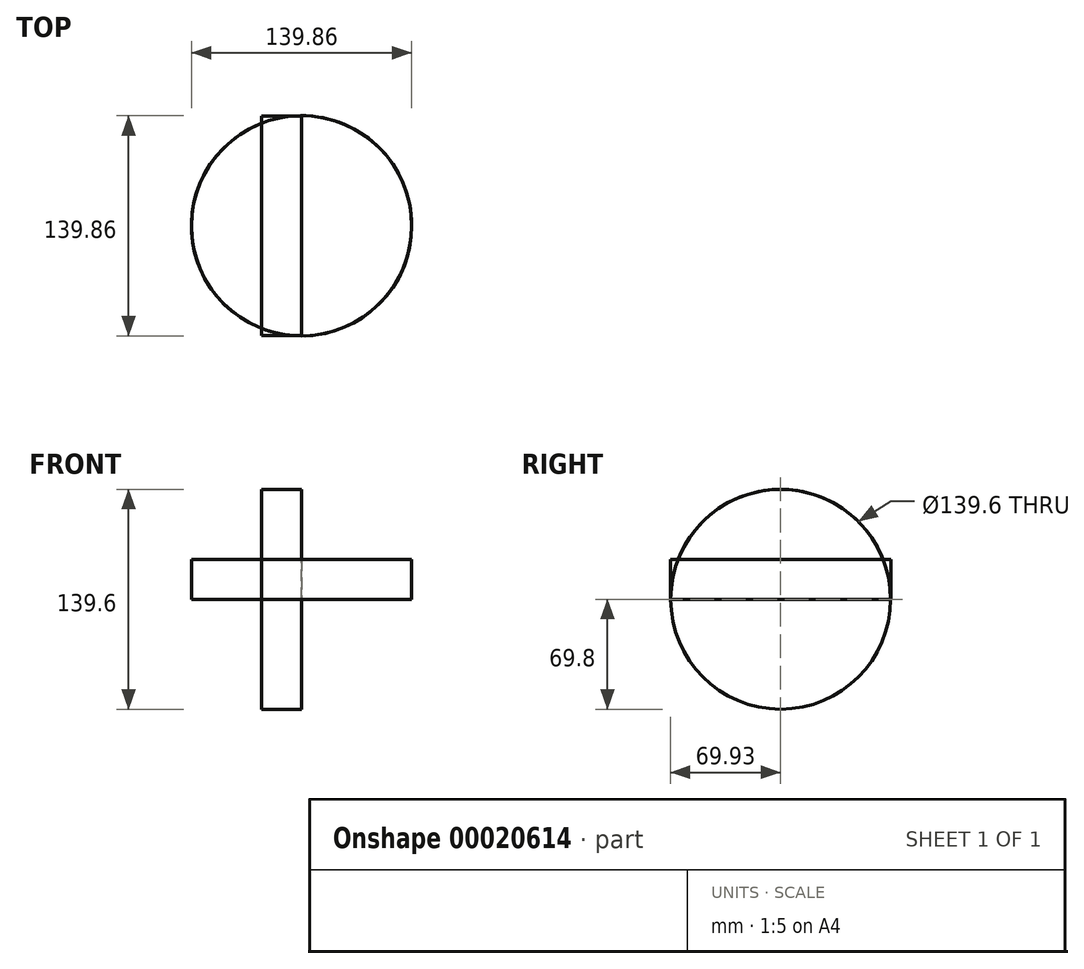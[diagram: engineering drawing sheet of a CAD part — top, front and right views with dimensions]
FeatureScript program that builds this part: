
annotation { "Feature Type Name" : "Feature", "Feature Type Description" : "" }
export const myFeature = defineFeature(function(context is Context, id is Id, definition is map)
    precondition{}
    {
        {
            var Q0;
            Q0=qCreatedBy(makeId("Top.planeOp"),FACE);
            var sketch = newSketch(context, id + "F0", { "sketchPlane" : qUnion([Q0])});
            skLineSegment(sketch, "E0", {"start": v(-76.27, 76.6) * mm, "end": v(75.98, 76.6) * mm});
            skLineSegment(sketch, "E1", {"start": v(75.98, 76.6) * mm, "end": v(75.98, -76.05) * mm});
            skLineSegment(sketch, "E2", {"start": v(75.98, -76.05) * mm, "end": v(-76.24, -76.05) * mm});
            skLineSegment(sketch, "E3", {"start": v(-76.24, -76.05) * mm, "end": v(-76.27, 76.6) * mm});
            skCircle(sketch, "E4", {"center": v(0, 0) * mm, "radius": 69.93 * mm});
            skSolve(sketch);
        }
        {
            var Q0;
            Q0=sQuery(id+"F0.wireOp",EDGE,"E4");
            extrude(context, id + "F1", {"bodyType" : ToolBodyType.SURFACE, "surfaceEntities" : qUnion([Q0]), "depth" : 25.4 * mm});
        }
        {
            var Q0;
            Q0=qCreatedBy(makeId("Right.planeOp"),FACE);
            var sketch = newSketch(context, id + "F2", { "sketchPlane" : qUnion([Q0])});
            skLineSegment(sketch, "E5", {"start": v(-76, 76.42) * mm, "end": v(75.92, 76.42) * mm});
            skLineSegment(sketch, "E6", {"start": v(75.92, 76.42) * mm, "end": v(75.92, -76.41) * mm});
            skLineSegment(sketch, "E7", {"start": v(75.92, -76.41) * mm, "end": v(-76.1, -76.41) * mm});
            skLineSegment(sketch, "E8", {"start": v(-76.1, -76.41) * mm, "end": v(-76, 76.42) * mm});
            skCircle(sketch, "E9", {"center": v(0, 0) * mm, "radius": 69.8 * mm});
            skSolve(sketch);
        }
        {
            var Q0;
            Q0=sQuery(id+"F2.wireOp",EDGE,"E9");
            extrude(context, id + "F3", {"bodyType" : ToolBodyType.SURFACE, "surfaceEntities" : qUnion([Q0]), "oppositeDirection" : true, "depth" : 25.4 * mm});
        }
    });
